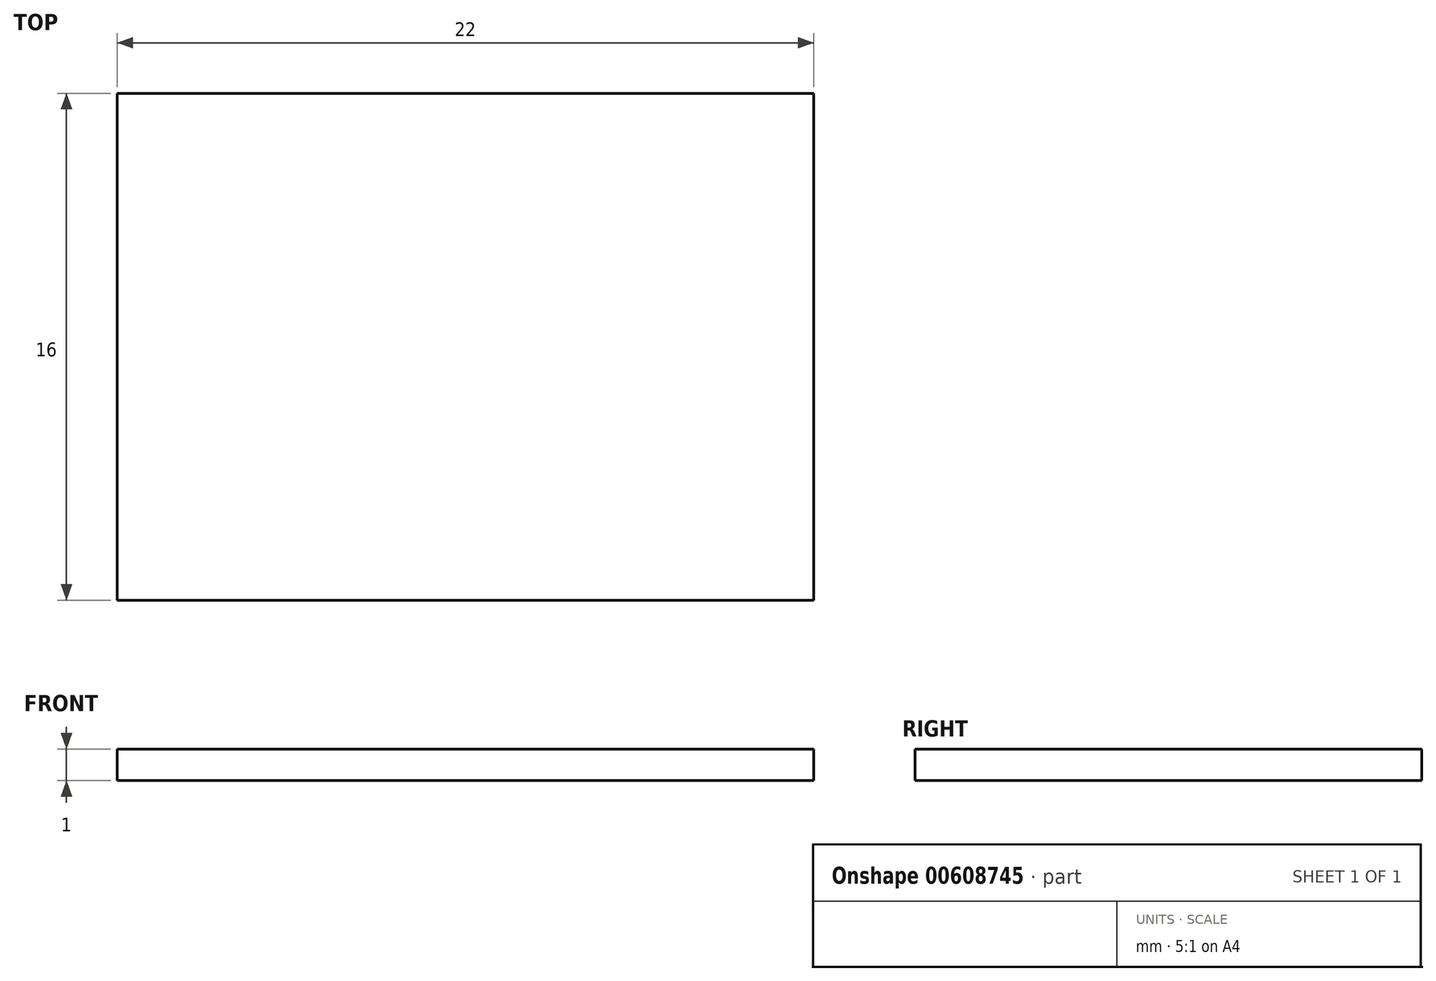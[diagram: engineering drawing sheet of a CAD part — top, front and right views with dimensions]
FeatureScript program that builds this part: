
annotation { "Feature Type Name" : "Feature", "Feature Type Description" : "" }
export const myFeature = defineFeature(function(context is Context, id is Id, definition is map)
    precondition{}
    {
        {
            var Q0;
            Q0=qCreatedBy(makeId("Top.planeOp"),FACE);
            var sketch = newSketch(context, id + "F0", { "sketchPlane" : qUnion([Q0])});
            skLineSegment(sketch, "E0.bottom", {"start": v(-34.91, 26.39) * mm, "end": v(-12.91, 26.39) * mm});
            skLineSegment(sketch, "E0.top", {"start": v(-34.91, 10.39) * mm, "end": v(-12.91, 10.39) * mm});
            skLineSegment(sketch, "E0.left", {"start": v(-34.91, 26.39) * mm, "end": v(-34.91, 10.39) * mm});
            skLineSegment(sketch, "E0.right", {"start": v(-12.91, 26.39) * mm, "end": v(-12.91, 10.39) * mm});
            skSolve(sketch);
        }
        {
            var Q0;
            Q0 = qSketchRegion(id + "F0", true);
            extrude(context, id + "F1", {"entities" : qUnion([Q0]), "depth" : 1 * mm, "offsetDistance" : 25 * mm});
        }
    });
